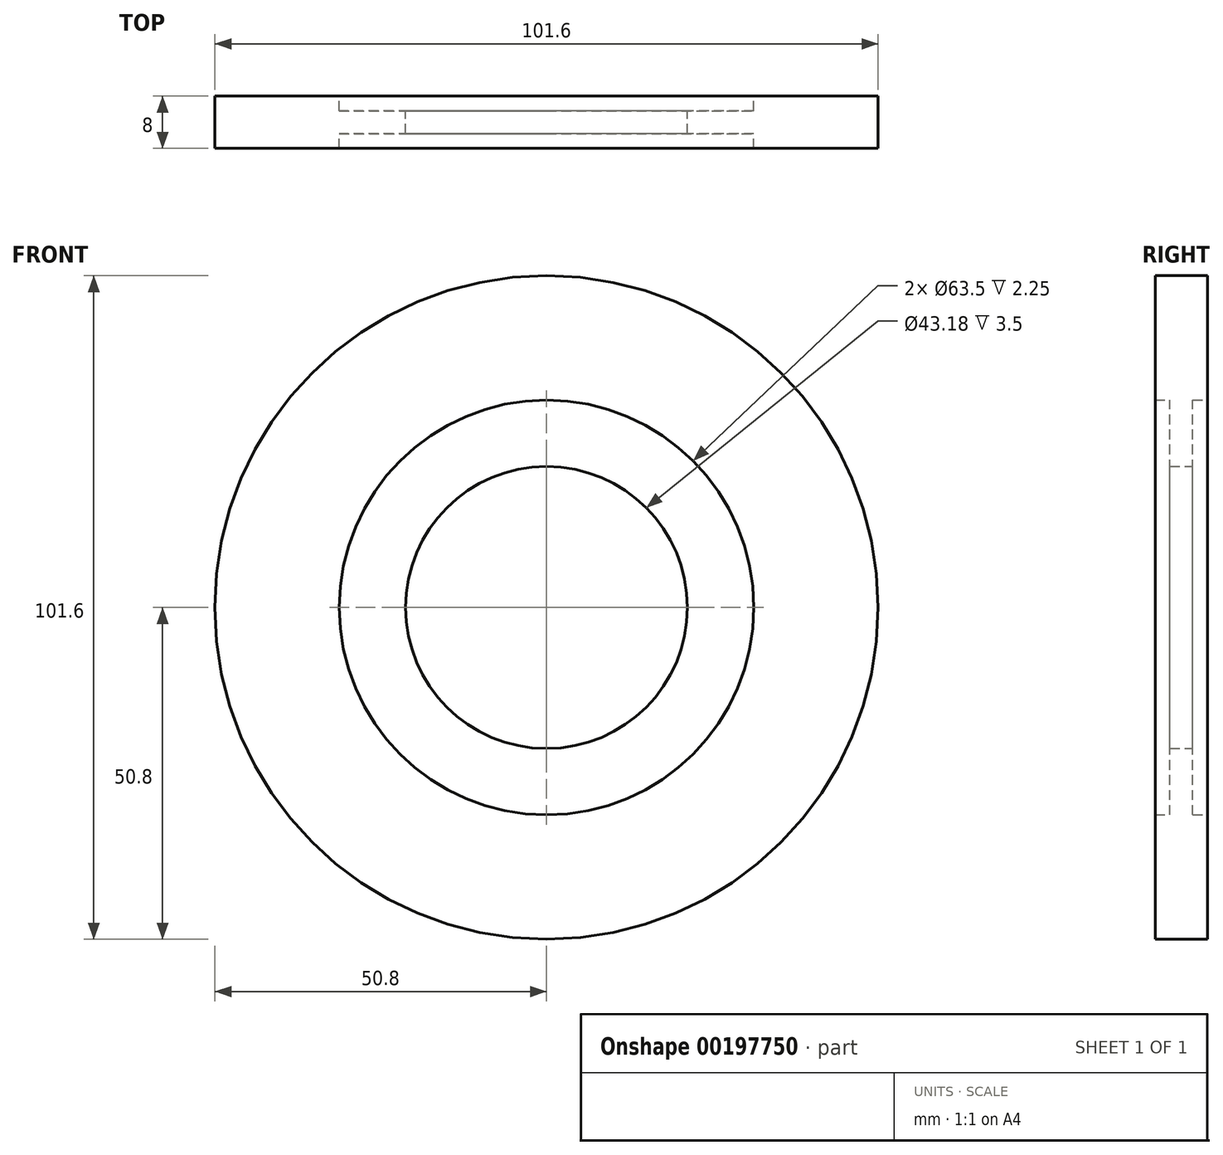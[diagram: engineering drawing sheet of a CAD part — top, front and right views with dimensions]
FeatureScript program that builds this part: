
annotation { "Feature Type Name" : "Feature", "Feature Type Description" : "" }
export const myFeature = defineFeature(function(context is Context, id is Id, definition is map)
    precondition{}
    {
        {
            assignVariable(context, id + "F0", {"name" : "LengthOutside", "anyValue" : 8});
        }
        {
            assignVariable(context, id + "F1", {"name" : "Depth", "anyValue" : 2.25});
        }
        {
            var Q0;
            Q0=qCreatedBy(makeId("Front.planeOp"),FACE);
            var sketch = newSketch(context, id + "F2", { "sketchPlane" : qUnion([Q0])});
            skCircle(sketch, "E0", {"center": v(0, 0) * mm, "radius": 21.59 * mm});
            skCircle(sketch, "E1", {"center": v(0, 0) * mm, "radius": 31.75 * mm});
            skCircle(sketch, "E2", {"center": v(0, 0) * mm, "radius": 50.8 * mm});
            skSolve(sketch);
        }
        {
            var Q0;
            Q0=makeQuery(id+"F2.imprint","IMPRINT",FACE,{"disambiguationData":[TD([[makeQuery(id+"F2.imprint","IMPRINT",EDGE,{"derivedFrom":sQuery(id+"F2.wireOp",EDGE,"E0")}),-1.0]])]});
            extrude(context, id + "F3", {"entities" : qUnion([Q0]), "depth" : (getVariable(context, 'LengthOutside') - (getVariable(context, 'Depth') * 2)) * mm, "symmetric" : true});
        }
        {
            var Q0;
            Q0 = qSketchRegion(id + "F2", true);
            var Q1;
            Q1=makeQuery(id+"F2.imprint","IMPRINT",FACE,{"disambiguationData":[TD([[makeQuery(id+"F2.imprint","IMPRINT",EDGE,{"derivedFrom":sQuery(id+"F2.wireOp",EDGE,"E1")}),-1.0]])]});
            extrude(context, id + "F4", {"entities" : qUnion([Q0, Q1]), "operationType" : NewBodyOperationType.ADD, "depth" : (getVariable(context, 'LengthOutside')) * mm, "symmetric" : true});
        }
    });
